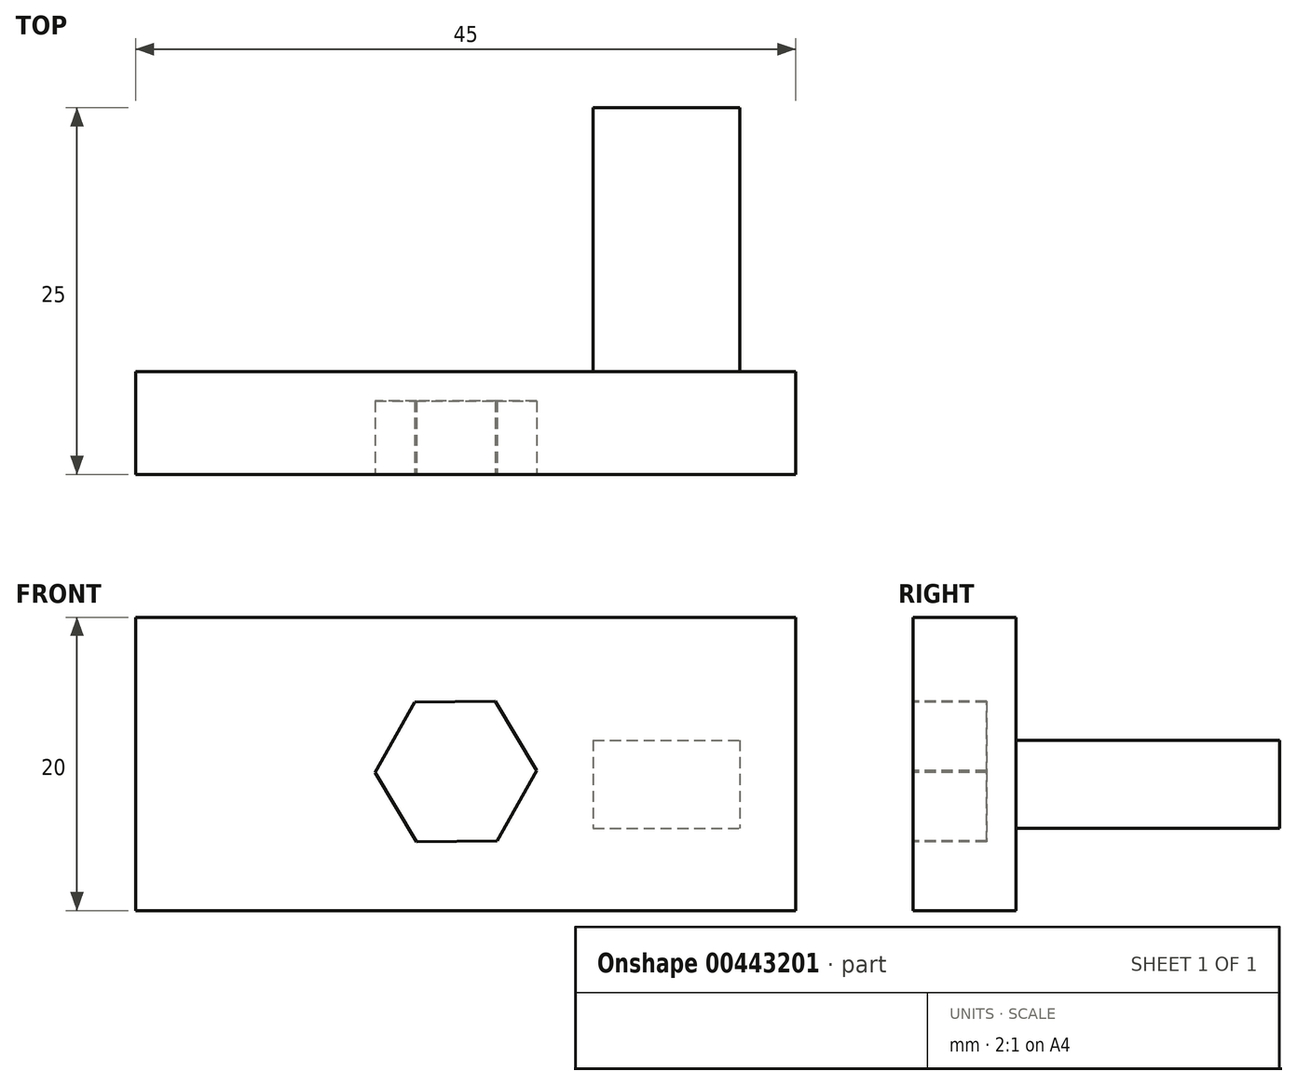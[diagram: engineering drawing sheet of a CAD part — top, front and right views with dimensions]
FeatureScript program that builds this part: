
annotation { "Feature Type Name" : "Feature", "Feature Type Description" : "" }
export const myFeature = defineFeature(function(context is Context, id is Id, definition is map)
    precondition{}
    {
        {
            var Q0;
            Q0=qCreatedBy(makeId("Front.planeOp"),FACE);
            var sketch = newSketch(context, id + "F0", { "sketchPlane" : qUnion([Q0])});
            skLineSegment(sketch, "E0.bottom", {"start": v(-21.84, 10.52) * mm, "end": v(23.16, 10.52) * mm});
            skLineSegment(sketch, "E0.top", {"start": v(-21.84, -9.48) * mm, "end": v(23.16, -9.48) * mm});
            skLineSegment(sketch, "E0.left", {"start": v(-21.84, 10.52) * mm, "end": v(-21.84, -9.48) * mm});
            skLineSegment(sketch, "E0.right", {"start": v(23.16, 10.52) * mm, "end": v(23.16, -9.48) * mm});
            skSolve(sketch);
        }
        {
            var Q0;
            Q0=makeQuery(id+"F0.imprint","IMPRINT",FACE,{"disambiguationData":[TD([[makeQuery(id+"F0.imprint","IMPRINT",EDGE,{"derivedFrom":sQuery(id+"F0.wireOp",EDGE,"E0.bottom")}),-1.0]])]});
            extrude(context, id + "F1", {"entities" : qUnion([Q0]), "depth" : 7 * mm});
        }
        {
            var Q0;
            Q0=makeQuery(id+"F1.opExtrude","CAP_FACE",FACE,{"disambiguationData":[OSD([sQuery(id+"F0.wireOp",EDGE,"E0.bottom"),sQuery(id+"F0.wireOp",EDGE,"E0.top"),sQuery(id+"F0.wireOp",EDGE,"E0.left"),sQuery(id+"F0.wireOp",EDGE,"E0.right")])],"isStart":false});
            var sketch = newSketch(context, id + "F2", { "sketchPlane" : qUnion([Q0])});
            skCircle(sketch, "E1.cCircle", {"center": v(0, 0) * mm, "radius": 4.76 * mm, "construction": true});
            skLineSegment(sketch, "E1.0", {"start": v(-5.5, -0.07) * mm, "end": v(-2.8, 4.73) * mm});
            skLineSegment(sketch, "E1.1", {"start": v(-2.8, 4.73) * mm, "end": v(2.7, 4.8) * mm});
            skLineSegment(sketch, "E1.2", {"start": v(2.7, 4.8) * mm, "end": v(5.5, 0.07) * mm});
            skLineSegment(sketch, "E1.3", {"start": v(5.5, 0.07) * mm, "end": v(2.8, -4.73) * mm});
            skLineSegment(sketch, "E1.4", {"start": v(2.8, -4.73) * mm, "end": v(-2.7, -4.8) * mm});
            skLineSegment(sketch, "E1.5", {"start": v(-2.7, -4.8) * mm, "end": v(-5.5, -0.07) * mm});
            skPoint(sketch, "E1.0.midPoint", {"position": v(-4.15, 2.33) * mm});
            skSolve(sketch);
        }
        {
            var Q0;
            Q0 = qSketchRegion(id + "F2", true);
            extrude(context, id + "F3", {"entities" : qUnion([Q0]), "operationType" : NewBodyOperationType.REMOVE, "oppositeDirection" : true, "depth" : 5 * mm});
        }
        {
            var Q0;
            Q0=makeQuery(id+"F1.opExtrude","CAP_FACE",FACE,{"disambiguationData":[OSD([sQuery(id+"F0.wireOp",EDGE,"E0.bottom"),sQuery(id+"F0.wireOp",EDGE,"E0.top"),sQuery(id+"F0.wireOp",EDGE,"E0.left"),sQuery(id+"F0.wireOp",EDGE,"E0.right")])],"isStart":false});
            var sketch = newSketch(context, id + "F4", { "sketchPlane" : qUnion([Q0])});
            skLineSegment(sketch, "E2.bottom", {"start": v(9.34, 2.14) * mm, "end": v(19.34, 2.14) * mm});
            skLineSegment(sketch, "E2.top", {"start": v(9.34, -3.86) * mm, "end": v(19.34, -3.86) * mm});
            skLineSegment(sketch, "E2.left", {"start": v(9.34, 2.14) * mm, "end": v(9.34, -3.86) * mm});
            skLineSegment(sketch, "E2.right", {"start": v(19.34, 2.14) * mm, "end": v(19.34, -3.86) * mm});
            skSolve(sketch);
        }
        {
            var Q0;
            Q0 = qSketchRegion(id + "F4", true);
            extrude(context, id + "F5", {"entities" : qUnion([Q0]), "operationType" : NewBodyOperationType.ADD, "oppositeDirection" : true, "depth" : 25 * mm, "offsetDistance" : 25 * mm});
        }
    });
